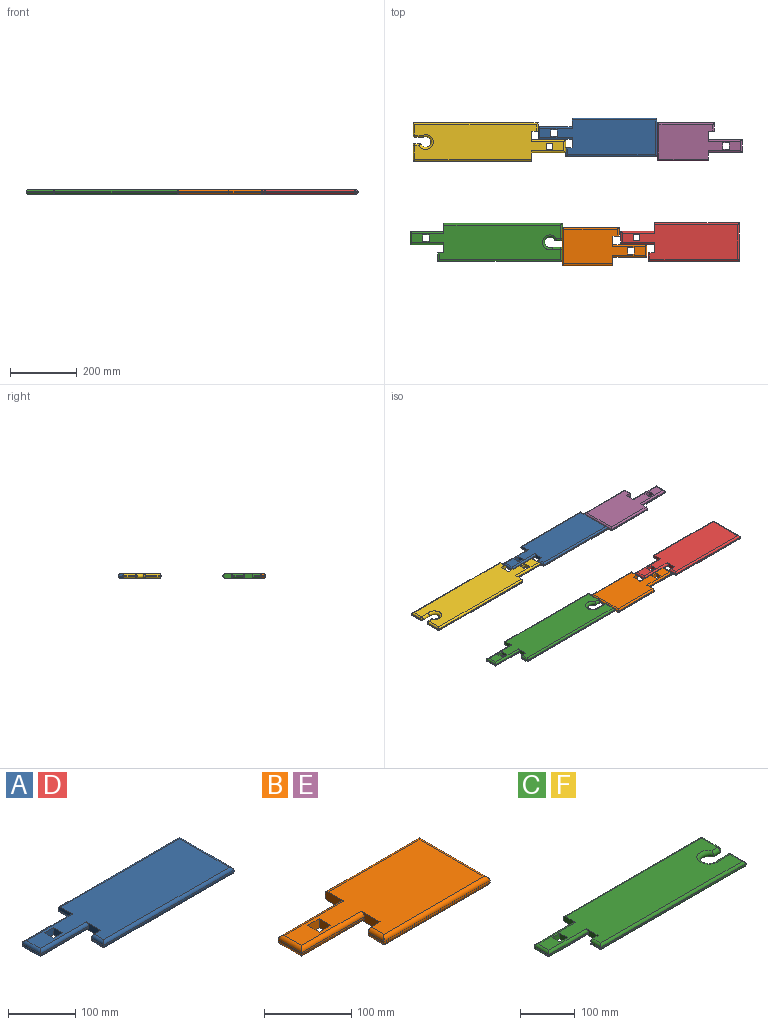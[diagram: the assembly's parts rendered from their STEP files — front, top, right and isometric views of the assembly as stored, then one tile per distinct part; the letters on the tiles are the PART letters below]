
ASSEMBLY  parts=6 mates=3
PART A: 31 faces, bbox 355.6x114.3x12.7 mm
  f0: plane 38.1x2.54mm, normal (-1,0,0), area 96.8mm2, adj f1,f13,f19,f29
  f1: plane 101.6x2.54mm, normal (0,-1,0), area 258.1mm2, adj f0,f2,f17,f30
  f2: plane 30.48x12.7mm, normal (-1,0,0), area 333.7mm2, adj f1,f3,f14,f15,f17,f30
  f3: plane 19.05x12.7mm, normal (0,1,0), area 230.9mm2, adj f2,f4,f14,f15,f16,f24
  f4: plane 25.4x2.54mm, normal (-1,0,0), area 64.5mm2, adj f3,f5,f16,f24
  f5: plane 273.05x2.54mm, normal (0,-1,0), area 693.5mm2, adj f4,f6,f18,f25
  f6: plane 114.3x2.54mm, normal (1,0,0), area 290.3mm2, adj f5,f7,f20,f26
  f7: plane 254x2.54mm, normal (0,1,0), area 645.2mm2, adj f6,f8,f22,f27
  f8: plane 30.48x7.62mm, normal (-1,0,0), area 193.5mm2, adj f7,f13,f14,f23,f27,f28
  f9: plane 19.05x12.7mm, normal (0,1,0), area 241.9mm2, adj f10,f12,f14,f15
  f10: plane 19.05x12.7mm, normal (1,0,0), area 241.9mm2, adj f9,f11,f14,f15
  f11: plane 19.05x12.7mm, normal (0,-1,0), area 241.9mm2, adj f10,f12,f14,f15
  f12: plane 19.05x12.7mm, normal (-1,0,0), area 241.9mm2, adj f9,f11,f14,f15
  f13: plane 101.6x2.54mm, normal (0,1,0), area 258.1mm2, adj f0,f8,f21,f28
  f14: plane 345.44x104.14mm, normal (0,0,1), area 28540.3mm2, adj f2,f3,f8,f9,f10,f11,f12,f24
  f15: plane 345.44x104.14mm, normal (0,0,-1), area 28411.2mm2, adj f2,f3,f9,f10,f11,f12,f16,f17
  f16: cylinder r=5.08mm len=25.4mm, axis (0,-1,0), area 188mm2, adj f3,f4,f15,f18
  f17: cylinder r=5.08mm len=101.6mm, axis (1,0,0), area 796mm2, adj f1,f2,f15,f19
  f18: cylinder r=5.08mm len=273.05mm, axis (1,0,0), area 2149.4mm2, adj f5,f15,f16,f20
  f19: cylinder r=5.08mm len=38.1mm, axis (0,-1,0), area 274.6mm2, adj f0,f15,f17,f21
  f20: cylinder r=5.08mm len=114.3mm, axis (0,1,0), area 882.6mm2, adj f6,f15,f18,f22
  f21: cylinder r=5.08mm len=106.68mm, axis (-1,0,0), area 810.7mm2, adj f13,f15,f19,f23
  f22: cylinder r=5.08mm len=254mm, axis (-1,0,0), area 1997.4mm2, adj f7,f15,f20,f23
  f23: cylinder r=5.08mm len=30.48mm, axis (0,-1,0), area 202.7mm2, adj f8,f15,f21,f22
  f24: cylinder r=5.08mm len=25.4mm, axis (0,1,0), area 188mm2, adj f3,f4,f14,f25
  f25: cylinder r=5.08mm len=273.05mm, axis (-1,0,0), area 2149.4mm2, adj f5,f14,f24,f26
  f26: cylinder r=5.08mm len=114.3mm, axis (0,-1,0), area 882.6mm2, adj f6,f14,f25,f27
  f27: cylinder r=5.08mm len=254mm, axis (1,0,0), area 2012.1mm2, adj f7,f8,f14,f26
  f28: cylinder r=5.08mm len=101.6mm, axis (1,0,0), area 796mm2, adj f8,f13,f14,f29
  f29: cylinder r=5.08mm len=38.1mm, axis (0,1,0), area 274.6mm2, adj f0,f14,f28,f30
  f30: cylinder r=5.08mm len=101.6mm, axis (-1,0,0), area 796mm2, adj f1,f2,f14,f29
PART B: 30 faces, bbox 254x114.3x12.7 mm
  f0: plane 38.1x2.54mm, normal (-1,0,0), area 96.8mm2, adj f1,f13,f21,f28
  f1: plane 101.6x2.54mm, normal (0,-1,0), area 258.1mm2, adj f0,f2,f22,f29
  f2: plane 30.48x12.7mm, normal (-1,0,0), area 333.7mm2, adj f1,f3,f14,f15,f22,f29
  f3: plane 19.05x12.7mm, normal (0,1,0), area 230.9mm2, adj f2,f4,f14,f15,f16,f23
  f4: plane 25.4x2.54mm, normal (-1,0,0), area 64.5mm2, adj f3,f5,f16,f23
  f5: plane 171.45x2.54mm, normal (0,-1,0), area 435.5mm2, adj f4,f6,f17,f24
  f6: plane 114.3x2.54mm, normal (1,0,0), area 290.3mm2, adj f5,f7,f18,f25
  f7: plane 152.4x2.54mm, normal (0,1,0), area 387.1mm2, adj f6,f8,f19,f26
  f8: plane 30.48x12.7mm, normal (-1,0,0), area 322.6mm2, adj f7,f13,f14,f15,f19,f20,f26,f27
  f9: plane 19.05x12.7mm, normal (0,1,0), area 241.9mm2, adj f10,f12,f14,f15
  f10: plane 19.05x12.7mm, normal (1,0,0), area 241.9mm2, adj f9,f11,f14,f15
  f11: plane 19.05x12.7mm, normal (0,-1,0), area 241.9mm2, adj f10,f12,f14,f15
  f12: plane 19.05x12.7mm, normal (-1,0,0), area 241.9mm2, adj f9,f11,f14,f15
  f13: plane 101.6x2.54mm, normal (0,1,0), area 258.1mm2, adj f0,f8,f20,f27
  f14: plane 243.84x104.14mm, normal (0,0,1), area 17959.6mm2, adj f2,f3,f8,f9,f10,f11,f12,f23
  f15: plane 243.84x104.14mm, normal (0,0,-1), area 17959.6mm2, adj f2,f3,f8,f9,f10,f11,f12,f16
  f16: cylinder r=5.08mm len=25.4mm, axis (0,-1,0), area 188mm2, adj f3,f4,f15,f17
  f17: cylinder r=5.08mm len=171.45mm, axis (1,0,0), area 1338.6mm2, adj f5,f15,f16,f18
  f18: cylinder r=5.08mm len=114.3mm, axis (0,1,0), area 882.6mm2, adj f6,f15,f17,f19
  f19: cylinder r=5.08mm len=152.4mm, axis (-1,0,0), area 1201.4mm2, adj f7,f8,f15,f18
  f20: cylinder r=5.08mm len=101.6mm, axis (-1,0,0), area 796mm2, adj f8,f13,f15,f21
  f21: cylinder r=5.08mm len=38.1mm, axis (0,-1,0), area 274.6mm2, adj f0,f15,f20,f22
  f22: cylinder r=5.08mm len=101.6mm, axis (1,0,0), area 796mm2, adj f1,f2,f15,f21
  f23: cylinder r=5.08mm len=25.4mm, axis (0,1,0), area 188mm2, adj f3,f4,f14,f24
  f24: cylinder r=5.08mm len=171.45mm, axis (-1,0,0), area 1338.6mm2, adj f5,f14,f23,f25
  f25: cylinder r=5.08mm len=114.3mm, axis (0,-1,0), area 882.6mm2, adj f6,f14,f24,f26
  f26: cylinder r=5.08mm len=152.4mm, axis (1,0,0), area 1201.4mm2, adj f7,f8,f14,f25
  f27: cylinder r=5.08mm len=101.6mm, axis (1,0,0), area 796mm2, adj f8,f13,f14,f28
  f28: cylinder r=5.08mm len=38.1mm, axis (0,1,0), area 274.6mm2, adj f0,f14,f27,f29
  f29: cylinder r=5.08mm len=101.6mm, axis (-1,0,0), area 796mm2, adj f1,f2,f14,f28
PART C: 38 faces, bbox 457.2x114.3x12.7 mm
  f0: plane 37.46x2.54mm, normal (1,0,0), area 94.5mm2, adj f8,f24,f25,f26
  f1: plane 447.04x104.14mm, normal (0,0,-1), area 37132.4mm2, adj f5,f6,f11,f12,f13,f14,f15,f17
  f2: plane 101.6x2.54mm, normal (0,1,0), area 258.1mm2, adj f3,f15,f32,f35
  f3: plane 38.1x2.54mm, normal (-1,0,0), area 96.8mm2, adj f2,f4,f33,f36
  f4: plane 101.6x2.54mm, normal (0,-1,0), area 258.1mm2, adj f3,f5,f34,f37
  f5: plane 30.48x12.7mm, normal (-1,0,0), area 333.7mm2, adj f1,f4,f6,f16,f34,f37
  f6: plane 19.05x12.7mm, normal (0,1,0), area 230.9mm2, adj f1,f5,f7,f16,f20,f21
  f7: plane 25.4x2.54mm, normal (-1,0,0), area 64.5mm2, adj f6,f8,f20,f21
  f8: plane 374.65x2.54mm, normal (0,-1,0), area 951.6mm2, adj f0,f7,f22,f23
  f9: plane 47.63x2.54mm, normal (1,0,0), area 120.3mm2, adj f10,f29,f30,f31
  f10: plane 355.6x2.54mm, normal (0,1,0), area 903.2mm2, adj f9,f15,f27,f28
  f11: plane 19.05x12.7mm, normal (0,1,0), area 241.9mm2, adj f1,f12,f14,f16
  f12: plane 19.05x12.7mm, normal (1,0,0), area 241.9mm2, adj f1,f11,f13,f16
  f13: plane 19.05x12.7mm, normal (0,-1,0), area 241.9mm2, adj f1,f12,f14,f16
  f14: plane 19.05x12.7mm, normal (-1,0,0), area 241.9mm2, adj f1,f11,f13,f16
  f15: plane 30.48x12.7mm, normal (-1,0,0), area 322.6mm2, adj f1,f2,f10,f16,f27,f28,f32,f35
  f16: plane 447.04x104.14mm, normal (0,0,1), area 37132.4mm2, adj f5,f6,f11,f12,f13,f14,f15,f17
  f17: cylinder r=6.35mm len=17.78mm, axis (1,0,0), area 322.9mm2, adj f1,f16,f18,f31
  f18: torus R=22.23mm, axis (0,0,1), area 1706.9mm2, adj f1,f16,f17,f19
  f19: cylinder r=6.35mm len=26.81mm, axis (-1,0,0), area 526.1mm2, adj f1,f16,f18,f26
  f20: cylinder r=5.08mm len=25.4mm, axis (0,-1,0), area 188mm2, adj f1,f6,f7,f22
  f21: cylinder r=5.08mm len=25.4mm, axis (0,1,0), area 188mm2, adj f6,f7,f16,f23
  f22: cylinder r=5.08mm len=374.65mm, axis (1,0,0), area 2960.1mm2, adj f1,f8,f20,f24
  f23: cylinder r=5.08mm len=374.65mm, axis (-1,0,0), area 2960.1mm2, adj f8,f16,f21,f25
  f24: cylinder r=5.08mm len=36.19mm, axis (0,1,0), area 274mm2, adj f0,f1,f22,f26
  f25: cylinder r=5.08mm len=36.19mm, axis (0,-1,0), area 274mm2, adj f0,f16,f23,f26
  f26: torus R=1.27mm, axis (1,0,0), area 112.9mm2, adj f0,f19,f24,f25
  f27: cylinder r=5.08mm len=355.6mm, axis (1,0,0), area 2822.8mm2, adj f10,f15,f16,f29
  f28: cylinder r=5.08mm len=355.6mm, axis (-1,0,0), area 2822.8mm2, adj f1,f10,f15,f30
  f29: cylinder r=5.08mm len=46.36mm, axis (0,-1,0), area 355.2mm2, adj f9,f16,f27,f31
  f30: cylinder r=5.08mm len=46.36mm, axis (0,1,0), area 355.2mm2, adj f1,f9,f28,f31
  f31: torus R=1.27mm, axis (1,0,0), area 112.9mm2, adj f9,f17,f29,f30
  f32: cylinder r=5.08mm len=101.6mm, axis (-1,0,0), area 796mm2, adj f1,f2,f15,f33
  f33: cylinder r=5.08mm len=38.1mm, axis (0,-1,0), area 274.6mm2, adj f1,f3,f32,f34
  f34: cylinder r=5.08mm len=101.6mm, axis (1,0,0), area 796mm2, adj f1,f4,f5,f33
  f35: cylinder r=5.08mm len=101.6mm, axis (1,0,0), area 796mm2, adj f2,f15,f16,f36
  f36: cylinder r=5.08mm len=38.1mm, axis (0,1,0), area 274.6mm2, adj f3,f16,f35,f37
  f37: cylinder r=5.08mm len=101.6mm, axis (-1,0,0), area 796mm2, adj f4,f5,f16,f36
PART D: same geometry as A
PART E: same geometry as B
PART F: same geometry as C
PLACE A t=(-247.13,313.7,0)mm
PLACE B rot(axis=(0,0,1),180deg) t=(-311.02,774.63,0)mm
PLACE C rot(axis=(0,0,-1),0deg) t=(-631.4,303.71,0)mm
PLACE D at identity
PLACE E rot(axis=(0,0,-1),180deg) t=(-25.57,1088.91,0)mm
PLACE F rot(axis=(0,0,1),180deg) t=(-554.42,633.73,0)mm
MATE parallel F.f0 <-> D.f6  axis (-1,0,0) through (-816.96,676.27,6.35)mm
MATE parallel C.f10 <-> B.f5  axis (0,1,0) through (-368.86,375.47,7.62)mm
MATE parallel A.f1 <-> E.f1  axis (0,-1,0) through (-390.99,626.75,6.35)mm
